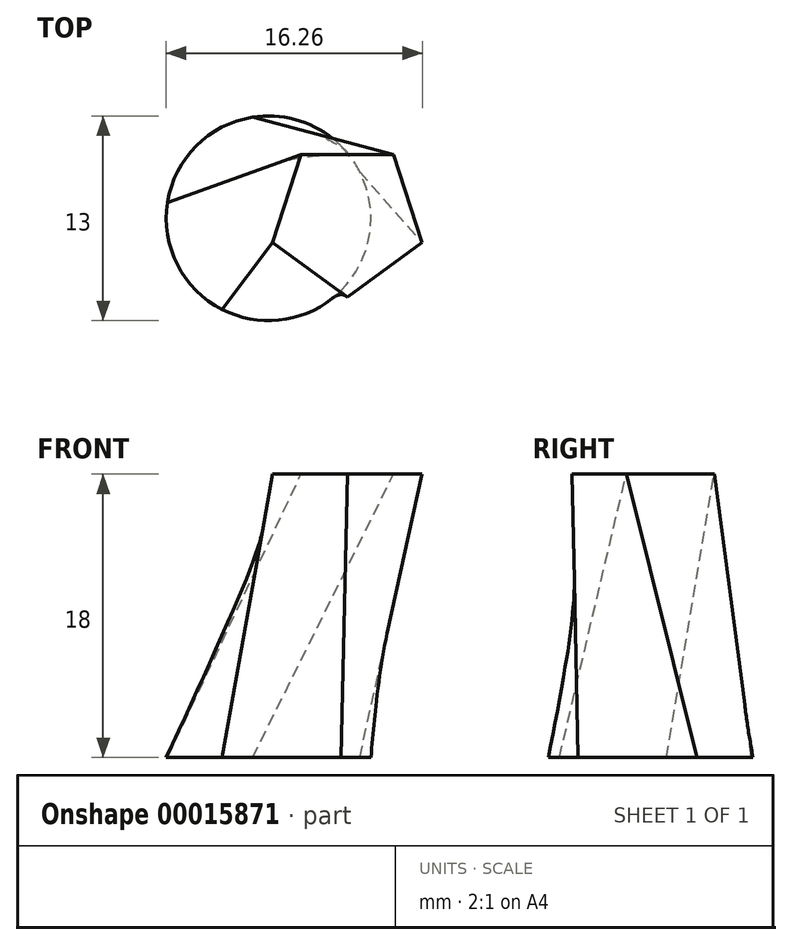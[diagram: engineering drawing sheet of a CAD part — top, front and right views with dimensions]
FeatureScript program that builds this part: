
annotation { "Feature Type Name" : "Feature", "Feature Type Description" : "" }
export const myFeature = defineFeature(function(context is Context, id is Id, definition is map)
    precondition{}
    {
        {
            var Q0;
            Q0=qCreatedBy(makeId("Top.planeOp"),FACE);
            var sketch = newSketch(context, id + "F0", { "sketchPlane" : qUnion([Q0])});
            skCircle(sketch, "E0", {"center": v(0, 0) * mm, "radius": 6.5 * mm});
            skSolve(sketch);
        }
        {
            var Q0;
            Q0=qCreatedBy(makeId("Front.planeOp"),FACE);
            var sketch = newSketch(context, id + "F1", { "sketchPlane" : qUnion([Q0])});
            skFitSpline(sketch, "E1", {"points": [v(0, 0) * mm, v(-2.7, 6.77) * mm, v(5, 18) * mm], "startDerivative": vector(-10.55, 15.3) * mm, "endDerivative": vector(19.03, 20.44) * mm});
            skSolve(sketch);
        }
        {
            var Q0;
            Q0=qCreatedBy(makeId("Top.planeOp"),FACE);
            cPlane(context, id + "F2", {"entities" : qUnion([Q0]), "cplaneType" : CPlaneType.OFFSET, "offset" : 18 * mm, "width" : 152.4 * mm, "height" : 152.4 * mm});
        }
        {
            var Q0;
            Q0=qCreatedBy(id+"F2.planeOp",FACE);
            var sketch = newSketch(context, id + "F3", { "sketchPlane" : qUnion([Q0])});
            skCircle(sketch, "E2.cCircle", {"center": v(5, 0) * mm, "radius": 5 * mm, "construction": true});
            skLineSegment(sketch, "E2.0", {"start": v(5, -5) * mm, "end": v(0.24, -1.55) * mm});
            skLineSegment(sketch, "E2.1", {"start": v(0.24, -1.55) * mm, "end": v(2.06, 4.05) * mm});
            skLineSegment(sketch, "E2.2", {"start": v(2.06, 4.05) * mm, "end": v(7.94, 4.05) * mm});
            skLineSegment(sketch, "E2.3", {"start": v(7.94, 4.05) * mm, "end": v(9.76, -1.55) * mm});
            skLineSegment(sketch, "E2.4", {"start": v(9.76, -1.55) * mm, "end": v(5, -5) * mm});
            skSolve(sketch);
        }
        {
            var Q0;
            Q0=makeQuery(id+"F0.imprint","IMPRINT",FACE,{"disambiguationData":[TD([[makeQuery(id+"F0.imprint","IMPRINT",EDGE,{"derivedFrom":sQuery(id+"F0.wireOp",EDGE,"E0")}),1.0]])]});
            var Q1;
            Q1=makeQuery(id+"F3.imprint","IMPRINT",FACE,{"disambiguationData":[TD([[makeQuery(id+"F3.imprint","IMPRINT",EDGE,{"derivedFrom":sQuery(id+"F3.wireOp",EDGE,"E2.0")}),-1.0]])]});
            var Q2;
            Q2=sQuery(id+"F1.wireOp",EDGE,"E1");
            loft(context, id + "F4", {"sheetProfilesArray" : [{ "sheetProfileEntities" : qUnion([Q0]) }, { "sheetProfileEntities" : qUnion([Q1]) }], "guidesArray" : [{ "guideEntities" : qUnion([Q2]), "guideDerivativeType" : LoftGuideDerivativeType.DEFAULT, "guideDerivativeMagnitude" : 1 }]});
        }
    });
